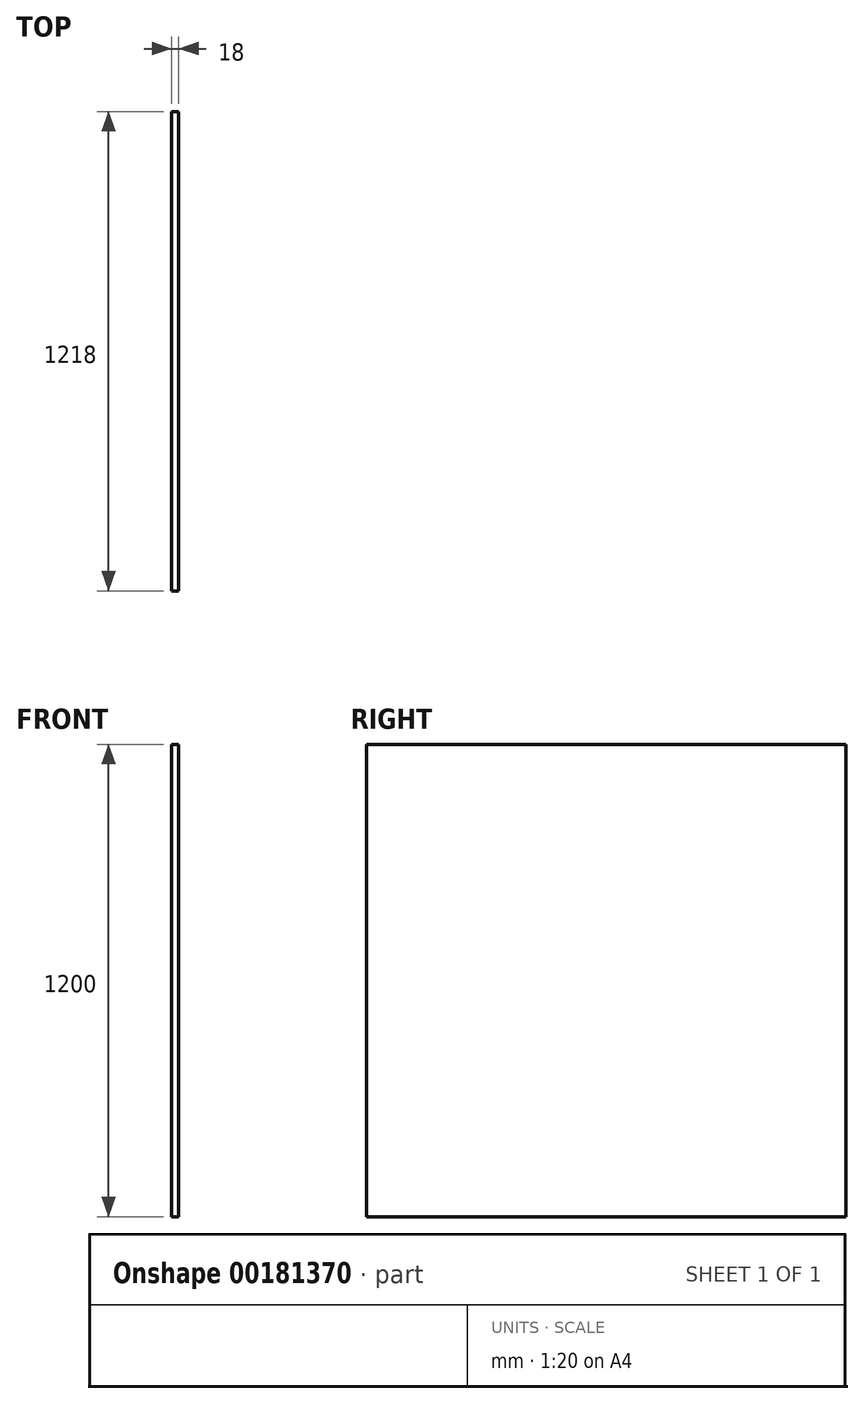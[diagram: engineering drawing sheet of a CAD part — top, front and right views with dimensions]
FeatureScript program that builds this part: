
annotation { "Feature Type Name" : "Feature", "Feature Type Description" : "" }
export const myFeature = defineFeature(function(context is Context, id is Id, definition is map)
    precondition{}
    {
        {
            var Q0;
            Q0=qCreatedBy(makeId("Right.planeOp"),FACE);
            var sketch = newSketch(context, id + "F0", { "sketchPlane" : qUnion([Q0])});
            skLineSegment(sketch, "E0.bottom", {"start": v(-609, 600) * mm, "end": v(609, 600) * mm});
            skLineSegment(sketch, "E0.top", {"start": v(-609, -600) * mm, "end": v(609, -600) * mm});
            skLineSegment(sketch, "E0.left", {"start": v(-609, 600) * mm, "end": v(-609, -600) * mm});
            skLineSegment(sketch, "E0.right", {"start": v(609, 600) * mm, "end": v(609, -600) * mm});
            skPoint(sketch, "E0.middle", {"position": v(0, 0) * mm});
            skSolve(sketch);
        }
        {
            var Q0;
            Q0 = qSketchRegion(id + "F0", true);
            extrude(context, id + "F1", {"entities" : qUnion([Q0]), "depth" : 18 * mm});
        }
    });
